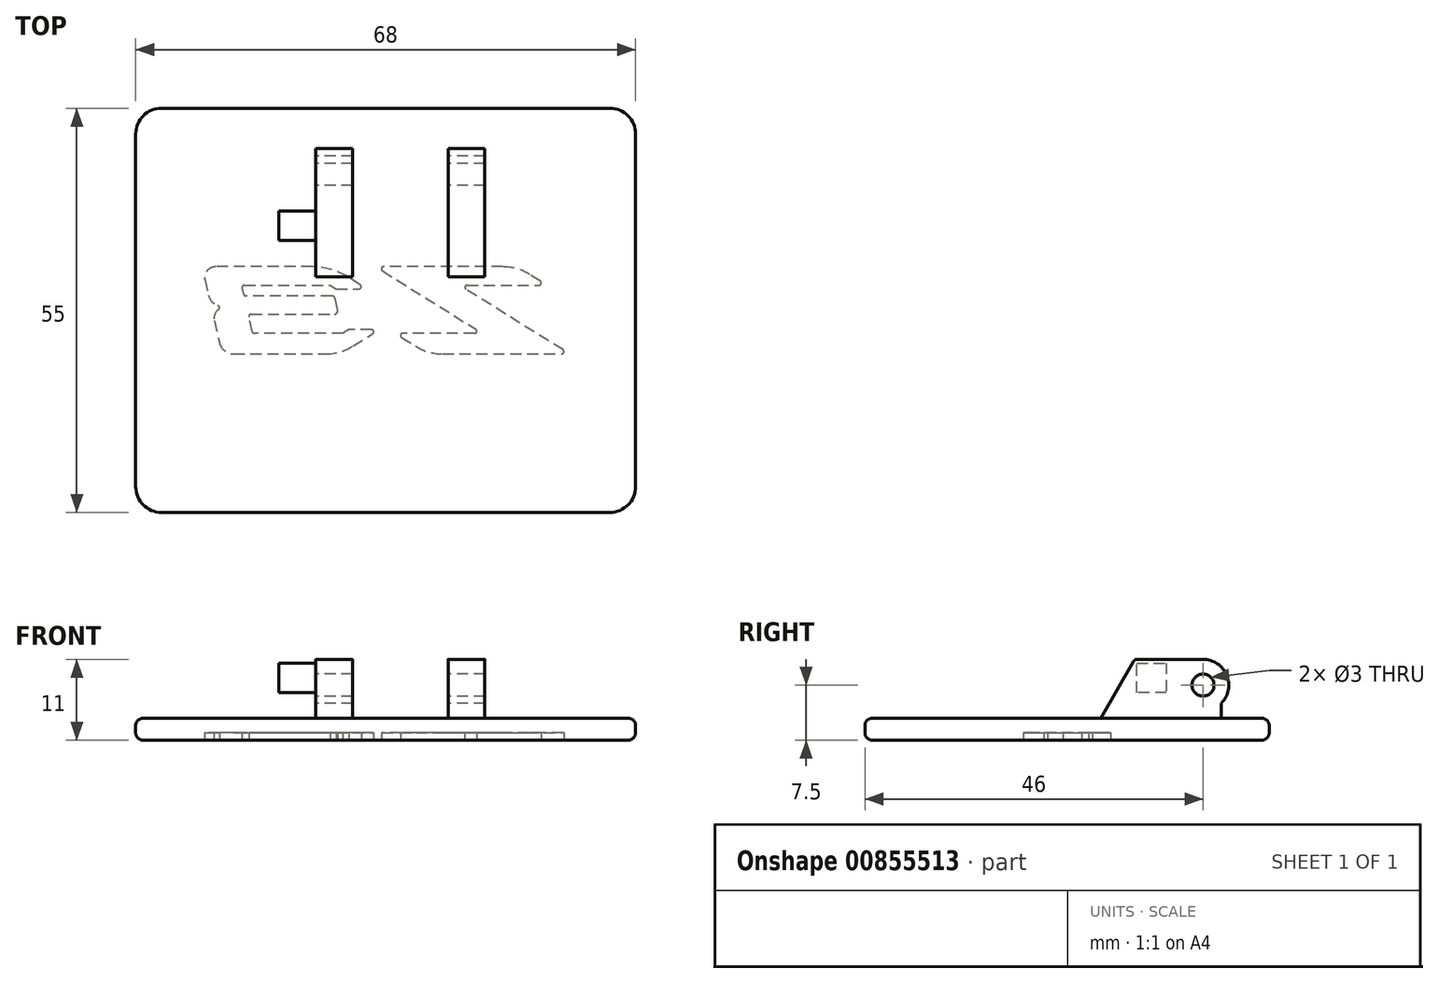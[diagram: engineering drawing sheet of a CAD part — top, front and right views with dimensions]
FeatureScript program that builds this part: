
annotation { "Feature Type Name" : "Feature", "Feature Type Description" : "" }
export const myFeature = defineFeature(function(context is Context, id is Id, definition is map)
    precondition{}
    {
        {
            var Q0;
            Q0=qCreatedBy(makeId("Top.planeOp"),FACE);
            var sketch = newSketch(context, id + "F0", { "sketchPlane" : qUnion([Q0])});
            skLineSegment(sketch, "E0.bottom", {"start": v(-30.5, 27.5) * mm, "end": v(30.5, 27.5) * mm});
            skLineSegment(sketch, "E0.top", {"start": v(-30.5, -27.5) * mm, "end": v(30.5, -27.5) * mm});
            skLineSegment(sketch, "E0.left", {"start": v(-34, 24) * mm, "end": v(-34, -24) * mm});
            skLineSegment(sketch, "E0.right", {"start": v(34, 24) * mm, "end": v(34, -24) * mm});
            skPoint(sketch, "E1.visualSharp", {"position": v(-34, 27.5) * mm});
            skArc(sketch, "E1.filletArc", {"start": v(-30.5, 27.5) * mm, "mid": v(-32.97, 26.47) * mm, "end": v(-34, 24) * mm});
            skPoint(sketch, "E2.visualSharp", {"position": v(34, 27.5) * mm});
            skArc(sketch, "E2.filletArc", {"start": v(34, 24) * mm, "mid": v(32.97, 26.47) * mm, "end": v(30.5, 27.5) * mm});
            skPoint(sketch, "E3.visualSharp", {"position": v(-34, -27.5) * mm});
            skArc(sketch, "E3.filletArc", {"start": v(-34, -24) * mm, "mid": v(-32.97, -26.47) * mm, "end": v(-30.5, -27.5) * mm});
            skPoint(sketch, "E4.visualSharp", {"position": v(34, -27.5) * mm});
            skArc(sketch, "E4.filletArc", {"start": v(30.5, -27.5) * mm, "mid": v(32.97, -26.47) * mm, "end": v(34, -24) * mm});
            skSolve(sketch);
        }
        {
            var Q0;
            Q0 = qSketchRegion(id + "F0", true);
            extrude(context, id + "F1", {"entities" : qUnion([Q0]), "depth" : 3 * mm, "offsetDistance" : 25 * mm});
        }
        {
            var Q0;
            Q0=qCreatedBy(makeId("Right.planeOp"),FACE);
            var sketch = newSketch(context, id + "F2", { "sketchPlane" : qUnion([Q0])});
            skLineSegment(sketch, "E5.0.0", {"start": v(-24, 3) * mm, "end": v(-27.5, 3) * mm});
            skLineSegment(sketch, "E5.0.2", {"start": v(-27.5, 3) * mm, "end": v(-24, 3) * mm});
            skLineSegment(sketch, "E5.0.3", {"start": v(-24, 3) * mm, "end": v(24, 3) * mm});
            skLineSegment(sketch, "E5.0.4", {"start": v(24, 3) * mm, "end": v(27.5, 3) * mm});
            skLineSegment(sketch, "E5.0.6", {"start": v(27.5, 3) * mm, "end": v(24, 3) * mm});
            skLineSegment(sketch, "E5.0.7", {"start": v(24, 3) * mm, "end": v(-24, 3) * mm});
            skLineSegment(sketch, "E6.0.0", {"start": v(-27.5, 0) * mm, "end": v(-24, 0) * mm});
            skLineSegment(sketch, "E6.0.1", {"start": v(-24, 0) * mm, "end": v(24, 0) * mm});
            skLineSegment(sketch, "E6.0.2", {"start": v(24, 0) * mm, "end": v(27.5, 0) * mm});
            skLineSegment(sketch, "E6.0.4", {"start": v(27.5, 0) * mm, "end": v(24, 0) * mm});
            skLineSegment(sketch, "E6.0.5", {"start": v(24, 0) * mm, "end": v(-24, 0) * mm});
            skLineSegment(sketch, "E6.0.6", {"start": v(-24, 0) * mm, "end": v(-27.5, 0) * mm});
            skLineSegment(sketch, "E6.1", {"start": v(27.5, 3) * mm, "end": v(27.5, 0) * mm});
            skLineSegment(sketch, "E6.2", {"start": v(-27.5, 3) * mm, "end": v(-27.5, 0) * mm});
            skCircle(sketch, "E7", {"center": v(18.5, 7.5) * mm, "radius": 1.5 * mm});
            skArc(sketch, "E8", {"start": v(21, 5.05) * mm, "mid": v(21.73, 8.86) * mm, "end": v(18.5, 11) * mm});
            skLineSegment(sketch, "E9", {"start": v(21, 5.05) * mm, "end": v(21, 3) * mm});
            skLineSegment(sketch, "E10", {"start": v(18.5, 11) * mm, "end": v(9.5, 11) * mm});
            skLineSegment(sketch, "E11", {"start": v(9.07, 10.75) * mm, "end": v(4.6, 3) * mm});
            skLineSegment(sketch, "E12", {"start": v(13.5, 10.5) * mm, "end": v(13.5, 6.5) * mm});
            skLineSegment(sketch, "E13", {"start": v(13.5, 6.5) * mm, "end": v(9.5, 6.5) * mm});
            skLineSegment(sketch, "E14", {"start": v(9.5, 6.5) * mm, "end": v(9.5, 10.5) * mm});
            skLineSegment(sketch, "E15", {"start": v(9.5, 10.5) * mm, "end": v(13.5, 10.5) * mm});
            skArc(sketch, "E16", {"start": v(9.5, 11) * mm, "mid": v(9.25, 10.93) * mm, "end": v(9.07, 10.75) * mm});
            skSolve(sketch);
        }
        {
            var Q0;
            Q0=makeQuery(id+"F2.imprint","IMPRINT",FACE,{"disambiguationData":[TD([[makeQuery(id+"F2.imprint","IMPRINT",EDGE,{"derivedFrom":sQuery(id+"F2.wireOp",EDGE,"E7")}),-1.0]])]});
            var Q1;
            Q1=makeQuery(id+"F2.imprint","IMPRINT",FACE,{"disambiguationData":[TD([[makeQuery(id+"F2.imprint","IMPRINT",EDGE,{"derivedFrom":sQuery(id+"F2.wireOp",EDGE,"E12")}),-1.0]])]});
            var Q2;
            Q2=makeQuery(id+"F1.opExtrude","SWEPT_FACE",FACE,{"disambiguationData":[OSD([sQuery(id+"F0.wireOp",EDGE,"E0.right")])]});
            var Q3;
            Q3=makeQuery(id+"F1.opExtrude","SWEPT_FACE",FACE,{"disambiguationData":[OSD([sQuery(id+"F0.wireOp",EDGE,"E0.left")])]});
            extrude(context, id + "F3", {"entities" : qUnion([Q0, Q1]), "operationType" : NewBodyOperationType.ADD, "endBound" : BoundingType.UP_TO_SURFACE, "depth" : 25 * mm, "endBoundEntityFace" : qUnion([Q2]), "hasOffset" : true, "offsetDistance" : 20.5 * mm, "hasSecondDirection" : true, "secondDirectionBound" : SecondDirectionBoundingType.UP_TO_SURFACE, "secondDirectionOppositeDirection" : true, "secondDirectionDepth" : 25 * mm, "secondDirectionBoundEntityFace" : qUnion([Q3]), "hasSecondDirectionOffset" : true, "secondDirectionOffsetDistance" : 24.5 * mm});
        }
        {
            var Q0;
            Q0=makeQuery(id+"F2.imprint","IMPRINT",FACE,{"disambiguationData":[TD([[makeQuery(id+"F2.imprint","IMPRINT",EDGE,{"derivedFrom":sQuery(id+"F2.wireOp",EDGE,"E12")}),-1.0]])]});
            var Q1;
            Q1=makeQuery(id+"F3.opExtrude","CAP_FACE",FACE,{"disambiguationData":[OSD([sQuery(id+"F2.wireOp",EDGE,"E5.0.7"),sQuery(id+"F2.wireOp",EDGE,"E7"),sQuery(id+"F2.wireOp",EDGE,"E8"),sQuery(id+"F2.wireOp",EDGE,"E9"),sQuery(id+"F2.wireOp",EDGE,"E10"),sQuery(id+"F2.wireOp",EDGE,"E11"),sQuery(id+"F2.wireOp",EDGE,"E16")])],"isStart":true});
            extrude(context, id + "F4", {"entities" : qUnion([Q0]), "operationType" : NewBodyOperationType.ADD, "endBound" : BoundingType.UP_TO_SURFACE, "oppositeDirection" : true, "depth" : 25 * mm, "endBoundEntityFace" : qUnion([Q1]), "hasOffset" : true, "offsetDistance" : 5 * mm, "offsetOppositeDirection" : true});
        }
        {
            var Q0;
            Q0=makeQuery(id+"F2.imprint","IMPRINT",FACE,{"disambiguationData":[TD([[makeQuery(id+"F2.imprint","IMPRINT",EDGE,{"derivedFrom":sQuery(id+"F2.wireOp",EDGE,"E7")}),-1.0]])]});
            var Q1;
            Q1=makeQuery(id+"F2.imprint","IMPRINT",FACE,{"disambiguationData":[TD([[makeQuery(id+"F2.imprint","IMPRINT",EDGE,{"derivedFrom":sQuery(id+"F2.wireOp",EDGE,"E12")}),-1.0]])]});
            var Q2;
            Q2=makeQuery(id+"F3.opExtrude","CAP_FACE",FACE,{"disambiguationData":[OSD([sQuery(id+"F2.wireOp",EDGE,"E5.0.7"),sQuery(id+"F2.wireOp",EDGE,"E7"),sQuery(id+"F2.wireOp",EDGE,"E8"),sQuery(id+"F2.wireOp",EDGE,"E9"),sQuery(id+"F2.wireOp",EDGE,"E10"),sQuery(id+"F2.wireOp",EDGE,"E11"),sQuery(id+"F2.wireOp",EDGE,"E16")])],"isStart":false});
            var Q3;
            Q3=makeQuery(id+"F3.opExtrude","CAP_FACE",FACE,{"disambiguationData":[OSD([sQuery(id+"F2.wireOp",EDGE,"E5.0.7"),sQuery(id+"F2.wireOp",EDGE,"E7"),sQuery(id+"F2.wireOp",EDGE,"E8"),sQuery(id+"F2.wireOp",EDGE,"E9"),sQuery(id+"F2.wireOp",EDGE,"E10"),sQuery(id+"F2.wireOp",EDGE,"E11"),sQuery(id+"F2.wireOp",EDGE,"E16")])],"isStart":true});
            extrude(context, id + "F5", {"entities" : qUnion([Q0, Q1]), "operationType" : NewBodyOperationType.REMOVE, "endBound" : BoundingType.UP_TO_SURFACE, "depth" : 25 * mm, "endBoundEntityFace" : qUnion([Q2]), "hasOffset" : true, "offsetDistance" : 5 * mm, "hasSecondDirection" : true, "secondDirectionBound" : SecondDirectionBoundingType.UP_TO_SURFACE, "secondDirectionOppositeDirection" : true, "secondDirectionDepth" : 25 * mm, "secondDirectionBoundEntityFace" : qUnion([Q3]), "hasSecondDirectionOffset" : true, "secondDirectionOffsetDistance" : 5 * mm});
        }
        {
            var Q0;
            Q0=makeQuery(id+"F1.opExtrude","CAP_EDGE",EDGE,{"disambiguationData":[OSD([sQuery(id+"F0.wireOp",EDGE,"E0.top")])],"isStart":true});
            var Q1;
            Q1=makeQuery(id+"F1.opExtrude","CAP_EDGE",EDGE,{"disambiguationData":[OSD([sQuery(id+"F0.wireOp",EDGE,"E0.top")])],"isStart":false});
            fillet(context, id + "F6", {"entities" : qUnion([Q0, Q1]), "radius" : 1 * mm, "tangentPropagation" : true, "allowEdgeOverflow" : false});
        }
        {
            var Q0;
            Q0=makeQuery(id+"F1.opExtrude","CAP_FACE",FACE,{"disambiguationData":[OSD([sQuery(id+"F0.wireOp",EDGE,"E0.bottom"),sQuery(id+"F0.wireOp",EDGE,"E0.top"),sQuery(id+"F0.wireOp",EDGE,"E0.left"),sQuery(id+"F0.wireOp",EDGE,"E0.right"),sQuery(id+"F0.wireOp",EDGE,"E1.filletArc"),sQuery(id+"F0.wireOp",EDGE,"E2.filletArc"),sQuery(id+"F0.wireOp",EDGE,"E3.filletArc"),sQuery(id+"F0.wireOp",EDGE,"E4.filletArc")])],"isStart":true});
            var sketch = newSketch(context, id + "F7", { "sketchPlane" : qUnion([Q0])});
            skLineSegment(sketch, "E17", {"start": v(-25, -5.93) * mm, "end": v(-22.26, 5.93) * mm, "construction": true});
            skLineSegment(sketch, "E18", {"start": v(25, 3.13) * mm, "end": v(-25, 3.13) * mm, "construction": true});
            skLineSegment(sketch, "E19", {"start": v(-25, -3.43) * mm, "end": v(25, -3.43) * mm, "construction": true});
            skLineSegment(sketch, "E20", {"start": v(-20.18, -5.93) * mm, "end": v(-17.44, 5.93) * mm, "construction": true});
            skLineSegment(sketch, "E21", {"start": v(-25, 0.53) * mm, "end": v(25, 0.53) * mm, "construction": true});
            skLineSegment(sketch, "E22", {"start": v(-25, -1.97) * mm, "end": v(25, -1.97) * mm, "construction": true});
            skLineSegment(sketch, "E23", {"start": v(-1.33, -5.93) * mm, "end": v(17.64, 5.93) * mm, "construction": true});
            skLineSegment(sketch, "E24", {"start": v(6.03, -5.93) * mm, "end": v(25, 5.93) * mm, "construction": true});
            skLineSegment(sketch, "E25", {"start": v(-6.95, -1.97) * mm, "end": v(-6.37, 0.53) * mm, "construction": true});
            skLineSegment(sketch, "E26", {"start": v(-6.72, -2.93) * mm, "end": v(-2.57, -2.93) * mm, "construction": true});
            skLineSegment(sketch, "E27", {"start": v(-0.86, 2.63) * mm, "end": v(-5.01, 2.63) * mm, "construction": true});
            skLineSegment(sketch, "E28", {"start": v(-2.57, -2.93) * mm, "end": v(-7.37, -5.93) * mm, "construction": true});
            skLineSegment(sketch, "E29", {"start": v(-6.72, -2.93) * mm, "end": v(-7.52, -3.43) * mm, "construction": true});
            skLineSegment(sketch, "E30", {"start": v(-0.86, 2.63) * mm, "end": v(-6.14, 5.93) * mm, "construction": true});
            skLineSegment(sketch, "E31", {"start": v(5.75, 5.93) * mm, "end": v(1.27, 3.13) * mm, "construction": true});
            skLineSegment(sketch, "E32", {"start": v(21.92, -3.43) * mm, "end": v(17.92, -5.93) * mm, "construction": true});
            skLineSegment(sketch, "E33", {"start": v(-5.01, 2.63) * mm, "end": v(-5.81, 3.13) * mm, "construction": true});
            skSolve(sketch);
        }
        {
            var Q0;
            {var subQ0=sQuery(id+"F0.wireOp",EDGE,"E4.filletArc");var subQ1=sQuery(id+"F0.wireOp",EDGE,"E3.filletArc");var subQ2=sQuery(id+"F0.wireOp",EDGE,"E2.filletArc");var subQ3=sQuery(id+"F0.wireOp",EDGE,"E1.filletArc");var subQ4=sQuery(id+"F0.wireOp",EDGE,"E0.right");var subQ5=sQuery(id+"F0.wireOp",EDGE,"E0.left");var subQ6=sQuery(id+"F0.wireOp",EDGE,"E0.top");var subQ7=sQuery(id+"F0.wireOp",EDGE,"E0.bottom");var subQ8=makeQuery(id+"F1.opExtrude","CAP_FACE",FACE,{"disambiguationData":[OSD([subQ7,subQ6,subQ5,subQ4,subQ3,subQ2,subQ1,subQ0])],"isStart":true});Q0=makeQuery(id+"F7.imprint","IMPRINT",FACE,{"disambiguationData":[TD([[makeQuery(id+"F7.imprint","IMPRINT",EDGE,{"derivedFrom":makeQuery(id+"F6.opFillet","BLEND_EDGE",EDGE,{"blendedFrom":[makeQuery(id+"F1.opExtrude","CAP_EDGE",EDGE,{"disambiguationData":[OSD([subQ7])],"isStart":true}),subQ8],"blendedInto":[subQ8]})}),1.0]])]});}
            var sketch = newSketch(context, id + "F8", { "sketchPlane" : qUnion([Q0])});
            skLineSegment(sketch, "E34", {"start": v(21.03, -3.98) * mm, "end": v(19.62, -4.86) * mm});
            skLineSegment(sketch, "E35", {"start": v(15.9, -5.93) * mm, "end": v(-0.29, -5.93) * mm});
            skLineSegment(sketch, "E36", {"start": v(-0.45, -5.37) * mm, "end": v(12.27, 2.57) * mm});
            skLineSegment(sketch, "E37", {"start": v(12.11, 3.13) * mm, "end": v(2.32, 3.13) * mm});
            skLineSegment(sketch, "E38", {"start": v(2.16, 3.68) * mm, "end": v(4.05, 4.86) * mm});
            skLineSegment(sketch, "E39", {"start": v(7.76, 5.93) * mm, "end": v(23.95, 5.93) * mm});
            skLineSegment(sketch, "E40", {"start": v(24.11, 5.37) * mm, "end": v(10.92, -2.87) * mm});
            skLineSegment(sketch, "E41", {"start": v(11.07, -3.43) * mm, "end": v(20.87, -3.43) * mm});
            skLineSegment(sketch, "E42", {"start": v(-3.46, -3.48) * mm, "end": v(-5.18, -4.56) * mm});
            skLineSegment(sketch, "E43", {"start": v(-9.95, -5.93) * mm, "end": v(-23.11, -5.93) * mm});
            skLineSegment(sketch, "E44", {"start": v(-24.58, -4.1) * mm, "end": v(-24.12, -2.1) * mm});
            skLineSegment(sketch, "E45", {"start": v(-23.3, 1.42) * mm, "end": v(-22.62, 4.38) * mm});
            skLineSegment(sketch, "E46", {"start": v(-20.67, 5.93) * mm, "end": v(-8.15, 5.93) * mm});
            skLineSegment(sketch, "E47", {"start": v(-4.44, 4.86) * mm, "end": v(-1.75, 3.18) * mm});
            skLineSegment(sketch, "E48", {"start": v(-1.9, 2.63) * mm, "end": v(-5.01, 2.63) * mm});
            skLineSegment(sketch, "E49", {"start": v(-5.01, 2.63) * mm, "end": v(-5.81, 3.13) * mm});
            skLineSegment(sketch, "E50", {"start": v(-5.81, 3.13) * mm, "end": v(-17.85, 3.13) * mm});
            skLineSegment(sketch, "E51", {"start": v(-18.14, 2.9) * mm, "end": v(-18.6, 0.9) * mm});
            skLineSegment(sketch, "E52", {"start": v(-18.3, 0.53) * mm, "end": v(-7, 0.53) * mm});
            skLineSegment(sketch, "E53", {"start": v(-6.51, -0.08) * mm, "end": v(-6.86, -1.58) * mm});
            skLineSegment(sketch, "E54", {"start": v(-7.35, -1.97) * mm, "end": v(-19.02, -1.97) * mm});
            skLineSegment(sketch, "E55", {"start": v(-19.32, -2.2) * mm, "end": v(-19.51, -3.06) * mm});
            skLineSegment(sketch, "E56", {"start": v(-19.22, -3.43) * mm, "end": v(-7.52, -3.43) * mm});
            skLineSegment(sketch, "E57", {"start": v(-7.52, -3.43) * mm, "end": v(-6.72, -2.93) * mm});
            skLineSegment(sketch, "E58", {"start": v(-6.72, -2.93) * mm, "end": v(-3.62, -2.93) * mm});
            skPoint(sketch, "E59.visualSharp", {"position": v(25, 5.93) * mm});
            skArc(sketch, "E59.filletArc", {"start": v(24.11, 5.37) * mm, "mid": v(24.24, 5.71) * mm, "end": v(23.95, 5.93) * mm});
            skPoint(sketch, "E60.visualSharp", {"position": v(-1.33, -5.93) * mm});
            skArc(sketch, "E60.filletArc", {"start": v(-0.45, -5.37) * mm, "mid": v(-0.57, -5.71) * mm, "end": v(-0.29, -5.93) * mm});
            skPoint(sketch, "E61.visualSharp", {"position": v(1.27, 3.13) * mm});
            skArc(sketch, "E61.filletArc", {"start": v(2.16, 3.68) * mm, "mid": v(2.03, 3.35) * mm, "end": v(2.32, 3.13) * mm});
            skPoint(sketch, "E62.visualSharp", {"position": v(21.92, -3.43) * mm});
            skArc(sketch, "E62.filletArc", {"start": v(21.03, -3.98) * mm, "mid": v(21.16, -3.65) * mm, "end": v(20.87, -3.43) * mm});
            skPoint(sketch, "E63.visualSharp", {"position": v(10.03, -3.43) * mm});
            skArc(sketch, "E63.filletArc", {"start": v(10.92, -2.87) * mm, "mid": v(10.79, -3.21) * mm, "end": v(11.07, -3.43) * mm});
            skPoint(sketch, "E64.visualSharp", {"position": v(13.16, 3.13) * mm});
            skArc(sketch, "E64.filletArc", {"start": v(12.27, 2.57) * mm, "mid": v(12.4, 2.91) * mm, "end": v(12.11, 3.13) * mm});
            skPoint(sketch, "E65.visualSharp", {"position": v(-18.69, 0.53) * mm});
            skArc(sketch, "E65.filletArc", {"start": v(-18.6, 0.9) * mm, "mid": v(-18.54, 0.64) * mm, "end": v(-18.3, 0.53) * mm});
            skPoint(sketch, "E66.visualSharp", {"position": v(-18.09, 3.13) * mm});
            skArc(sketch, "E66.filletArc", {"start": v(-17.85, 3.13) * mm, "mid": v(-18.03, 3.06) * mm, "end": v(-18.14, 2.9) * mm});
            skPoint(sketch, "E67.visualSharp", {"position": v(-19.26, -1.97) * mm});
            skArc(sketch, "E67.filletArc", {"start": v(-19.02, -1.97) * mm, "mid": v(-19.21, -2.04) * mm, "end": v(-19.32, -2.2) * mm});
            skPoint(sketch, "E68.visualSharp", {"position": v(-19.6, -3.43) * mm});
            skArc(sketch, "E68.filletArc", {"start": v(-19.51, -3.06) * mm, "mid": v(-19.46, -3.31) * mm, "end": v(-19.22, -3.43) * mm});
            skPoint(sketch, "E69.visualSharp", {"position": v(-2.57, -2.93) * mm});
            skArc(sketch, "E69.filletArc", {"start": v(-3.46, -3.48) * mm, "mid": v(-3.33, -3.15) * mm, "end": v(-3.62, -2.93) * mm});
            skPoint(sketch, "E70.visualSharp", {"position": v(-0.86, 2.63) * mm});
            skArc(sketch, "E70.filletArc", {"start": v(-1.9, 2.63) * mm, "mid": v(-1.62, 2.85) * mm, "end": v(-1.75, 3.18) * mm});
            skPoint(sketch, "E71.visualSharp", {"position": v(5.75, 5.93) * mm});
            skArc(sketch, "E71.filletArc", {"start": v(7.76, 5.93) * mm, "mid": v(5.83, 5.66) * mm, "end": v(4.05, 4.86) * mm});
            skPoint(sketch, "E72.visualSharp", {"position": v(17.92, -5.93) * mm});
            skArc(sketch, "E72.filletArc", {"start": v(15.9, -5.93) * mm, "mid": v(17.84, -5.66) * mm, "end": v(19.62, -4.86) * mm});
            skPoint(sketch, "E73.visualSharp", {"position": v(-7.37, -5.93) * mm});
            skArc(sketch, "E73.filletArc", {"start": v(-9.95, -5.93) * mm, "mid": v(-7.47, -5.58) * mm, "end": v(-5.18, -4.56) * mm});
            skPoint(sketch, "E74.visualSharp", {"position": v(-6.14, 5.93) * mm});
            skArc(sketch, "E74.filletArc", {"start": v(-4.44, 4.86) * mm, "mid": v(-6.22, 5.66) * mm, "end": v(-8.15, 5.93) * mm});
            skPoint(sketch, "E75.visualSharp", {"position": v(-6.95, -1.97) * mm});
            skArc(sketch, "E75.filletArc", {"start": v(-7.35, -1.97) * mm, "mid": v(-7.03, -1.86) * mm, "end": v(-6.86, -1.58) * mm});
            skPoint(sketch, "E76.visualSharp", {"position": v(-6.37, 0.53) * mm});
            skArc(sketch, "E76.filletArc", {"start": v(-6.51, -0.08) * mm, "mid": v(-6.6, 0.34) * mm, "end": v(-7, 0.53) * mm});
            skPoint(sketch, "E77.visualSharp", {"position": v(-22.26, 5.93) * mm});
            skArc(sketch, "E77.filletArc", {"start": v(-20.67, 5.93) * mm, "mid": v(-21.92, 5.5) * mm, "end": v(-22.62, 4.38) * mm});
            skPoint(sketch, "E78.visualSharp", {"position": v(-25, -5.93) * mm});
            skArc(sketch, "E78.filletArc", {"start": v(-24.58, -4.1) * mm, "mid": v(-24.29, -5.36) * mm, "end": v(-23.11, -5.93) * mm});
            skArc(sketch, "E79", {"start": v(-23.3, 1.42) * mm, "mid": v(-23.25, 0.56) * mm, "end": v(-22.72, -0.13) * mm});
            skArc(sketch, "E80", {"start": v(-22.8, -0.66) * mm, "mid": v(-23.65, -1.2) * mm, "end": v(-24.12, -2.1) * mm});
            skArc(sketch, "E81", {"start": v(-22.8, -0.66) * mm, "mid": v(-22.6, -0.42) * mm, "end": v(-22.72, -0.13) * mm});
            skSolve(sketch);
        }
        {
            var Q0;
            Q0 = qSketchRegion(id + "F8", true);
            extrude(context, id + "F9", {"entities" : qUnion([Q0]), "operationType" : NewBodyOperationType.REMOVE, "oppositeDirection" : true, "depth" : 1 * mm, "offsetDistance" : 25 * mm});
        }
    });
